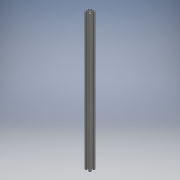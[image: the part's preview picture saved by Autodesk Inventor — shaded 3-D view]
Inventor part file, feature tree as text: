
AUTODESK INVENTOR PART (.ipt)
format: ipt  version: 2016 (Build 200138000, 138)  size: 272,384 bytes
history: native  units: mm
features: other x1, extrude x1, sketch x1
ambient origin geometry x8: Origin, YZ Plane, XZ Plane, XY Plane, X Axis, Y Axis, Z Axis, Center Point
bodies: Body1 (feature_tree)
feature tree (3):
  other  "Твердое тело1"
  extrude  "Выдавливание1"  Depth=0.25mm
  sketch  "Эскиз1"
